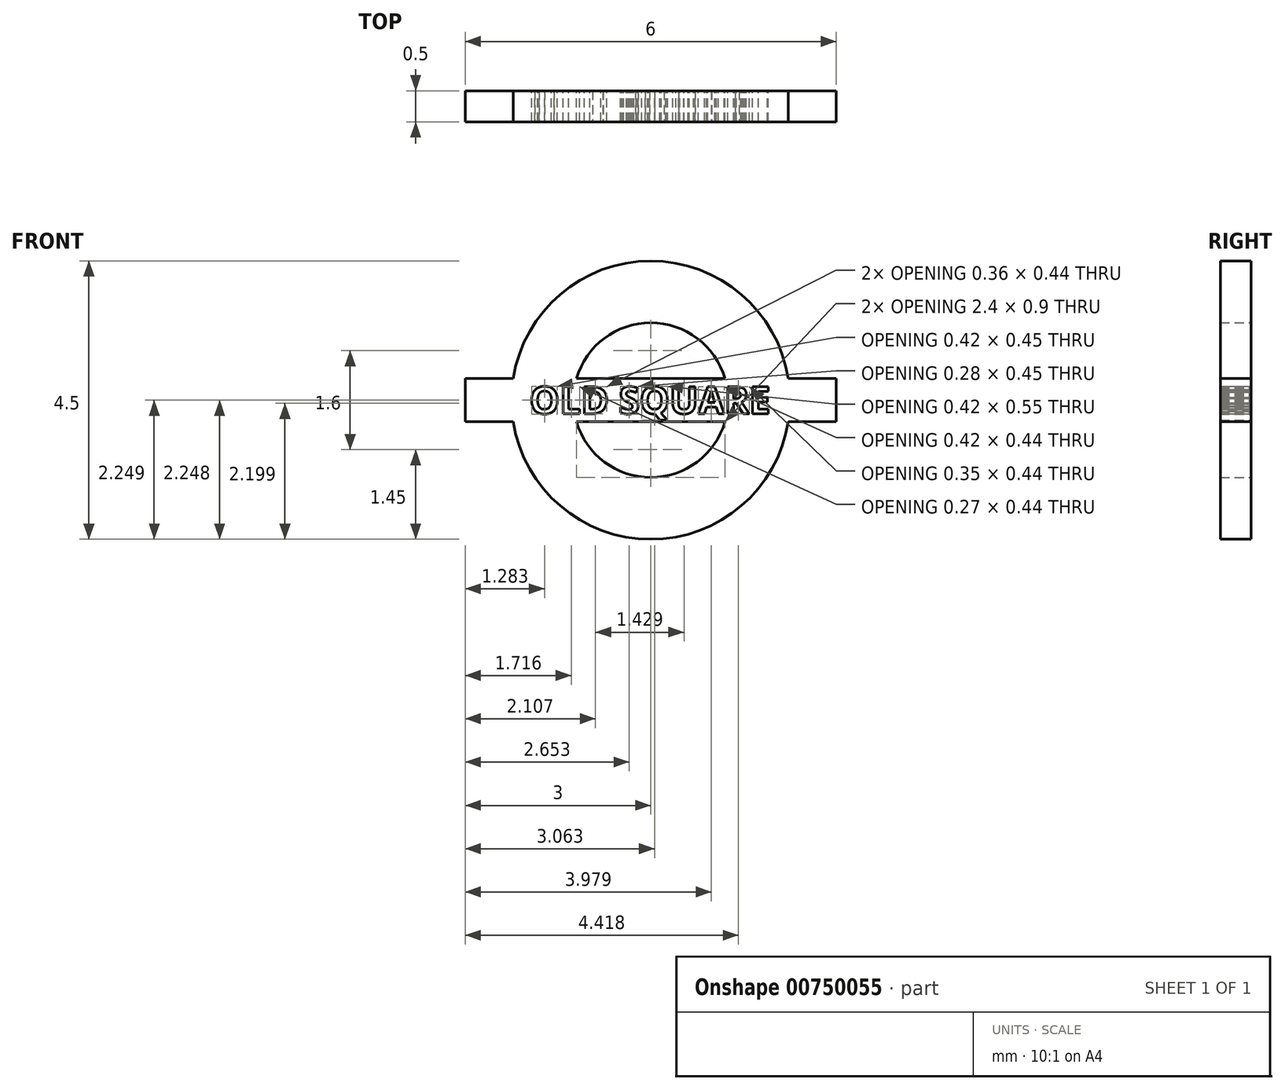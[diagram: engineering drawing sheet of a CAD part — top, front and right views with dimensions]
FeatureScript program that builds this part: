
annotation { "Feature Type Name" : "Feature", "Feature Type Description" : "" }
export const myFeature = defineFeature(function(context is Context, id is Id, definition is map)
    precondition{}
    {
        {
            var Q0;
            Q0=qCreatedBy(makeId("Front.planeOp"),FACE);
            var sketch = newSketch(context, id + "F0", { "sketchPlane" : qUnion([Q0])});
            skCircle(sketch, "E0", {"center": v(0, 0) * mm, "radius": 2.25 * mm});
            skCircle(sketch, "E1", {"center": v(0, 0) * mm, "radius": 1.25 * mm});
            skSolve(sketch);
        }
        {
            var Q0;
            Q0 = qSketchRegion(id + "F0", true);
            extrude(context, id + "F1", {"entities" : qUnion([Q0]), "depth" : 0.5 * mm, "offsetDistance" : 25.4 * mm});
        }
        {
            var Q0;
            Q0=qCreatedBy(makeId("Front.planeOp"),FACE);
            var sketch = newSketch(context, id + "F2", { "sketchPlane" : qUnion([Q0])});
            skPoint(sketch, "E2.middle", {"position": v(0, 0) * mm});
            skLineSegment(sketch, "E3.bottom", {"start": v(3, 0.35) * mm, "end": v(-3, 0.35) * mm});
            skLineSegment(sketch, "E3.top", {"start": v(3, -0.35) * mm, "end": v(-3, -0.35) * mm});
            skLineSegment(sketch, "E3.left", {"start": v(3, 0.35) * mm, "end": v(3, -0.35) * mm});
            skLineSegment(sketch, "E3.right", {"start": v(-3, 0.35) * mm, "end": v(-3, -0.35) * mm});
            skSolve(sketch);
        }
        {
            var Q0;
            Q0 = qSketchRegion(id + "F2", true);
            extrude(context, id + "F3", {"entities" : qUnion([Q0]), "operationType" : NewBodyOperationType.ADD, "depth" : 0.5 * mm, "offsetDistance" : 25.4 * mm});
        }
        {
            var Q0;
            Q0=qCreatedBy(makeId("Front.planeOp"),FACE);
            var sketch = newSketch(context, id + "F4", { "sketchPlane" : qUnion([Q0])});
            skText(sketch, "E4", { "text": "OLD SQUARE ", "fontName": "OpenSans-Bold.ttf"});
            const initialGuessF4  = {"E4": [-0.00196, -0.00022, 1, 0, 0.00044]};
            skSetInitialGuess(sketch, initialGuessF4);
            skSolve(sketch);
        }
        {
            var Q0;
            Q0 = qSketchRegion(id + "F4", true);
            extrude(context, id + "F5", {"entities" : qUnion([Q0]), "operationType" : NewBodyOperationType.REMOVE, "endBound" : BoundingType.UP_TO_NEXT, "depth" : 25.4 * mm, "offsetDistance" : 25.4 * mm});
        }
    });
